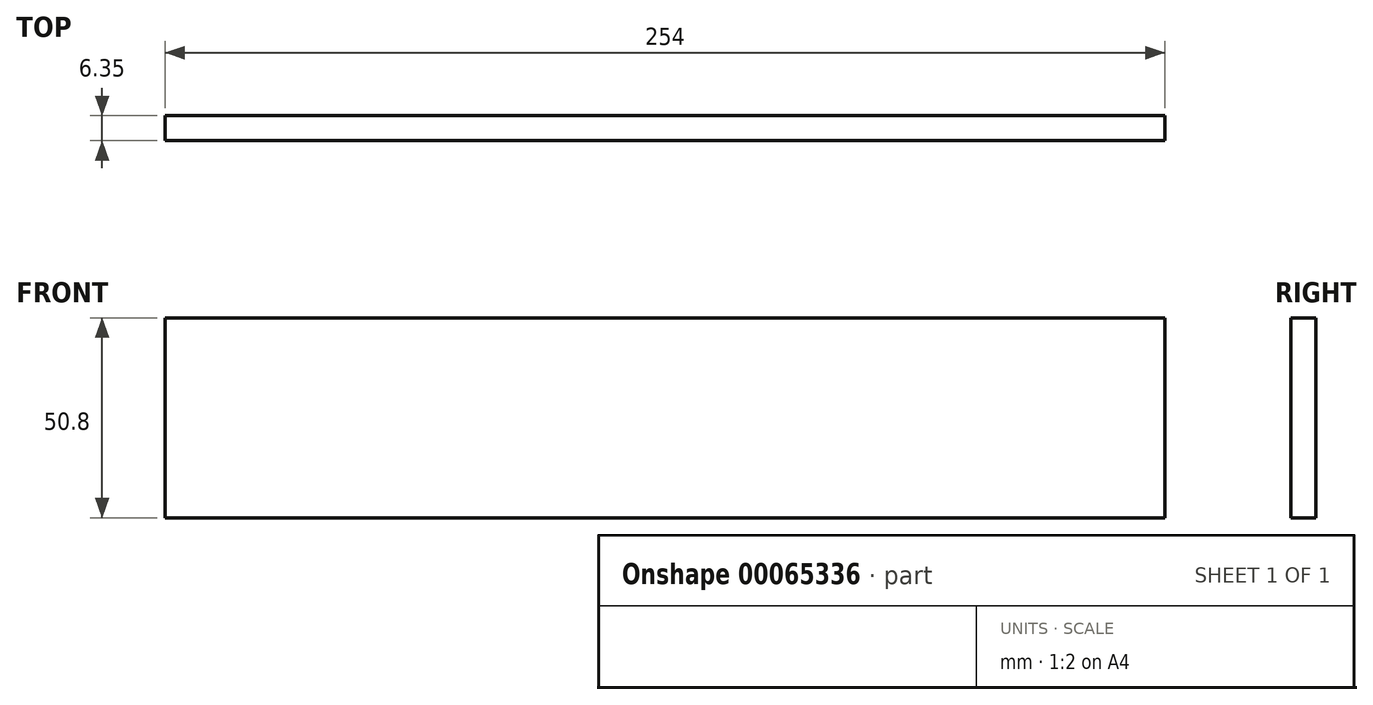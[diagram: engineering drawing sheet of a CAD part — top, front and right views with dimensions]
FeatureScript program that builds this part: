
annotation { "Feature Type Name" : "Feature", "Feature Type Description" : "" }
export const myFeature = defineFeature(function(context is Context, id is Id, definition is map)
    precondition{}
    {
        {
            var Q0;
            Q0=qCreatedBy(makeId("Front.planeOp"),FACE);
            var sketch = newSketch(context, id + "F0", { "sketchPlane" : qUnion([Q0])});
            skLineSegment(sketch, "E0.bottom", {"start": v(0, 0) * mm, "end": v(-254, 0) * mm});
            skLineSegment(sketch, "E0.top", {"start": v(0, -50.8) * mm, "end": v(-254, -50.8) * mm});
            skLineSegment(sketch, "E0.left", {"start": v(0, 0) * mm, "end": v(0, -50.8) * mm});
            skLineSegment(sketch, "E0.right", {"start": v(-254, 0) * mm, "end": v(-254, -50.8) * mm});
            skSolve(sketch);
        }
        {
            var Q0;
            Q0 = qSketchRegion(id + "F0", true);
            extrude(context, id + "F1", {"entities" : qUnion([Q0]), "depth" : 6.35 * mm});
        }
    });
